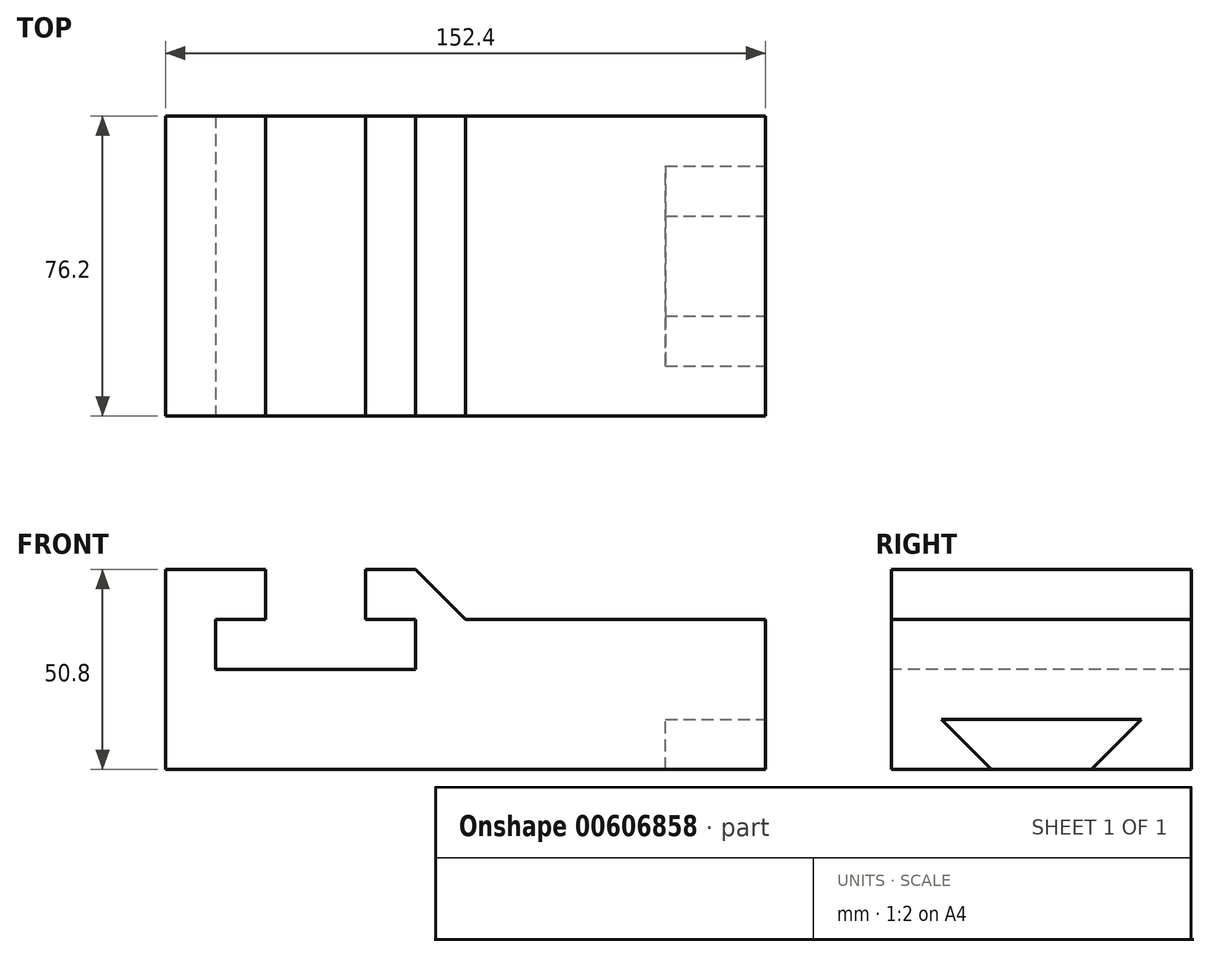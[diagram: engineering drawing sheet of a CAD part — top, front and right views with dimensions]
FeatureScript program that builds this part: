
annotation { "Feature Type Name" : "Feature", "Feature Type Description" : "" }
export const myFeature = defineFeature(function(context is Context, id is Id, definition is map)
    precondition{}
    {
        {
            var Q0;
            Q0=qCreatedBy(makeId("Front.planeOp"),FACE);
            var sketch = newSketch(context, id + "F0", { "sketchPlane" : qUnion([Q0])});
            skLineSegment(sketch, "E0", {"start": v(0, 0) * mm, "end": v(0, 50.8) * mm});
            skLineSegment(sketch, "E1", {"start": v(0, 50.8) * mm, "end": v(25.4, 50.8) * mm});
            skLineSegment(sketch, "E2", {"start": v(0, 0) * mm, "end": v(152.4, 0) * mm});
            skLineSegment(sketch, "E3", {"start": v(152.4, 0) * mm, "end": v(152.4, 38.1) * mm});
            skLineSegment(sketch, "E4", {"start": v(152.4, 38.1) * mm, "end": v(76.2, 38.1) * mm});
            skLineSegment(sketch, "E5", {"start": v(76.2, 38.1) * mm, "end": v(76.2, 50.8) * mm});
            skLineSegment(sketch, "E6", {"start": v(76.2, 50.8) * mm, "end": v(50.8, 50.8) * mm});
            skLineSegment(sketch, "E7", {"start": v(50.8, 50.8) * mm, "end": v(50.8, 38.1) * mm});
            skLineSegment(sketch, "E8", {"start": v(25.4, 50.8) * mm, "end": v(25.4, 38.1) * mm});
            skLineSegment(sketch, "E9", {"start": v(25.4, 38.1) * mm, "end": v(12.7, 38.1) * mm});
            skLineSegment(sketch, "E10", {"start": v(12.7, 38.1) * mm, "end": v(12.7, 25.4) * mm});
            skLineSegment(sketch, "E11", {"start": v(12.7, 25.4) * mm, "end": v(63.5, 25.4) * mm});
            skLineSegment(sketch, "E12", {"start": v(63.5, 25.4) * mm, "end": v(63.5, 38.16) * mm});
            skLineSegment(sketch, "E13", {"start": v(63.5, 38.16) * mm, "end": v(50.8, 38.1) * mm});
            skSolve(sketch);
        }
        {
            var Q0;
            Q0 = qSketchRegion(id + "F0", true);
            extrude(context, id + "F1", {"entities" : qUnion([Q0]), "oppositeDirection" : true, "depth" : 76.2 * mm, "offsetDistance" : 25.4 * mm});
        }
        {
            var Q0;
            Q0=makeQuery(id+"F1.opExtrude","SWEPT_FACE",FACE,{"disambiguationData":[OSD([sQuery(id+"F0.wireOp",EDGE,"E3")])]});
            var sketch = newSketch(context, id + "F2", { "sketchPlane" : qUnion([Q0])});
            skLineSegment(sketch, "E14", {"start": v(0, 0) * mm, "end": v(25.4, 0) * mm});
            skLineSegment(sketch, "E15", {"start": v(25.4, 0) * mm, "end": v(12.7, 12.7) * mm});
            skLineSegment(sketch, "E16", {"start": v(12.7, 12.7) * mm, "end": v(63.5, 12.7) * mm});
            skLineSegment(sketch, "E17", {"start": v(63.5, 12.7) * mm, "end": v(50.8, 0) * mm});
            skLineSegment(sketch, "E18", {"start": v(50.8, 0) * mm, "end": v(76.2, 0) * mm});
            skLineSegment(sketch, "E19", {"start": v(76.2, 0) * mm, "end": v(76.2, 38.1) * mm});
            skLineSegment(sketch, "E20", {"start": v(76.2, 38.1) * mm, "end": v(0, 38.1) * mm});
            skLineSegment(sketch, "E21", {"start": v(0, 38.1) * mm, "end": v(0, 0) * mm});
            skLineSegment(sketch, "E22", {"start": v(25.4, 0) * mm, "end": v(50.8, 0) * mm});
            skLineSegment(sketch, "E23", {"start": v(50.8, 0) * mm, "end": v(25.4, 0) * mm});
            skSolve(sketch);
        }
        {
            var Q0;
            Q0=makeQuery(id+"F2.imprint","IMPRINT",FACE,{"disambiguationData":[TD([[makeQuery(id+"F2.imprint","IMPRINT",EDGE,{"derivedFrom":sQuery(id+"F2.wireOp",EDGE,"E15")}),-1.0]])]});
            extrude(context, id + "F3", {"entities" : qUnion([Q0]), "operationType" : NewBodyOperationType.REMOVE, "oppositeDirection" : true, "depth" : 25.4 * mm, "offsetDistance" : 25.4 * mm});
        }
        {
            var Q0;
            Q0=makeQuery(id+"F1.opExtrude","CAP_FACE",FACE,{"disambiguationData":[OSD([sQuery(id+"F0.wireOp",EDGE,"E0"),sQuery(id+"F0.wireOp",EDGE,"E1"),sQuery(id+"F0.wireOp",EDGE,"E2"),sQuery(id+"F0.wireOp",EDGE,"E3"),sQuery(id+"F0.wireOp",EDGE,"E4"),sQuery(id+"F0.wireOp",EDGE,"E5"),sQuery(id+"F0.wireOp",EDGE,"E6"),sQuery(id+"F0.wireOp",EDGE,"E7"),sQuery(id+"F0.wireOp",EDGE,"E8"),sQuery(id+"F0.wireOp",EDGE,"E9"),sQuery(id+"F0.wireOp",EDGE,"E10"),sQuery(id+"F0.wireOp",EDGE,"E11"),sQuery(id+"F0.wireOp",EDGE,"E12"),sQuery(id+"F0.wireOp",EDGE,"E13")])],"isStart":true});
            var sketch = newSketch(context, id + "F4", { "sketchPlane" : qUnion([Q0])});
            skLineSegment(sketch, "E24", {"start": v(63.5, 50.8) * mm, "end": v(76.2, 38.1) * mm});
            skLineSegment(sketch, "E25", {"start": v(76.2, 38.1) * mm, "end": v(76.2, 50.8) * mm});
            skLineSegment(sketch, "E26", {"start": v(76.2, 50.8) * mm, "end": v(63.5, 50.8) * mm});
            skSolve(sketch);
        }
        {
            var Q0;
            Q0 = qSketchRegion(id + "F4", true);
            extrude(context, id + "F5", {"entities" : qUnion([Q0]), "operationType" : NewBodyOperationType.REMOVE, "oppositeDirection" : true, "depth" : 76.2 * mm, "offsetDistance" : 25.4 * mm});
        }
    });
